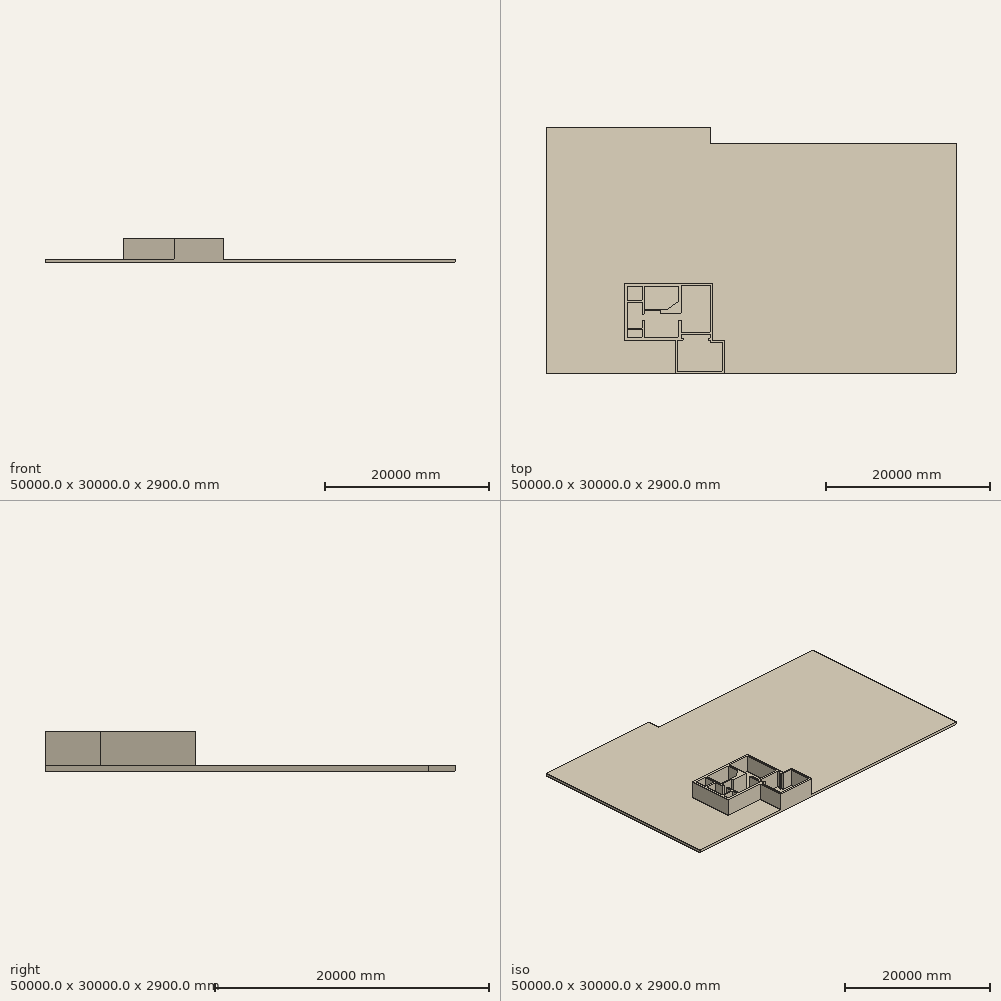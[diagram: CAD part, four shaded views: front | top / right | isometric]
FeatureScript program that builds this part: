
annotation { "Feature Type Name" : "Feature", "Feature Type Description" : "" }
export const myFeature = defineFeature(function(context is Context, id is Id, definition is map)
    precondition{}
    {
        {
            var Q0;
            Q0=qCreatedBy(makeId("Top.planeOp"),FACE);
            var sketch = newSketch(context, id + "F0", { "sketchPlane" : qUnion([Q0])});
            skLineSegment(sketch, "E0.bottom", {"start": v(-24996.8, 16240.64) * mm, "end": v(-4996.8, 16240.64) * mm});
            skLineSegment(sketch, "E0.top", {"start": v(-24996.8, -13759.36) * mm, "end": v(25003.2, -13759.36) * mm});
            skLineSegment(sketch, "E0.left", {"start": v(-24996.8, 16240.64) * mm, "end": v(-24996.8, -13759.36) * mm});
            skLineSegment(sketch, "E0.right", {"start": v(25003.2, 14240.64) * mm, "end": v(25003.2, -13759.36) * mm});
            skLineSegment(sketch, "E1", {"start": v(-4996.8, 16240.64) * mm, "end": v(-4996.8, 14240.64) * mm});
            skLineSegment(sketch, "E2", {"start": v(-4996.8, 14240.64) * mm, "end": v(25003.2, 14240.64) * mm});
            skSolve(sketch);
        }
        {
            var Q0;
            Q0 = qSketchRegion(id + "F0", true);
            extrude(context, id + "F1", {"entities" : qUnion([Q0]), "oppositeDirection" : true, "depth" : 400 * mm});
        }
        {
            var Q0;
            Q0=makeQuery(id+"F1.opExtrude","CAP_FACE",FACE,{"disambiguationData":[OSD([sQuery(id+"F0.wireOp",EDGE,"E0.bottom"),sQuery(id+"F0.wireOp",EDGE,"E0.top"),sQuery(id+"F0.wireOp",EDGE,"E0.left"),sQuery(id+"F0.wireOp",EDGE,"E0.right"),sQuery(id+"F0.wireOp",EDGE,"E1"),sQuery(id+"F0.wireOp",EDGE,"E2")])],"isStart":true});
            var sketch = newSketch(context, id + "F2", { "sketchPlane" : qUnion([Q0])});
            skLineSegment(sketch, "E3.bottom", {"start": v(-15496.8, -2759.36) * mm, "end": v(-8546.8, -2759.36) * mm});
            skLineSegment(sketch, "E3.top", {"start": v(-15496.8, -9759.36) * mm, "end": v(-8546.8, -9759.36) * mm});
            skLineSegment(sketch, "E3.left", {"start": v(-15496.8, -2759.36) * mm, "end": v(-15496.8, -9759.36) * mm});
            skLineSegment(sketch, "E3.right", {"start": v(-4796.8, -2759.36) * mm, "end": v(-4796.8, -9759.36) * mm});
            skLineSegment(sketch, "E4.bottom", {"start": v(-9246.8, -9759.36) * mm, "end": v(-8546.8, -9759.36) * mm});
            skLineSegment(sketch, "E4.top", {"start": v(-9246.8, -13759.36) * mm, "end": v(-3246.8, -13759.36) * mm});
            skLineSegment(sketch, "E4.left", {"start": v(-9246.8, -9759.36) * mm, "end": v(-9246.8, -13759.36) * mm});
            skLineSegment(sketch, "E4.right", {"start": v(-3246.8, -9759.36) * mm, "end": v(-3246.8, -13759.36) * mm});
            skLineSegment(sketch, "E5", {"start": v(-8546.8, -3009.36) * mm, "end": v(-8546.8, -6409.36) * mm});
            skLineSegment(sketch, "E6.trimOffspring", {"start": v(-4796.8, -9759.36) * mm, "end": v(-3246.8, -9759.36) * mm});
            skLineSegment(sketch, "E7.0", {"start": v(-15146.8, -3109.36) * mm, "end": v(-13346.8, -3109.36) * mm});
            skLineSegment(sketch, "E7.1", {"start": v(-15146.8, -3109.36) * mm, "end": v(-15146.8, -4909.36) * mm});
            skLineSegment(sketch, "E7.2", {"start": v(-15146.8, -9409.36) * mm, "end": v(-13346.8, -9409.36) * mm});
            skLineSegment(sketch, "E7.3", {"start": v(-8896.8, -3109.36) * mm, "end": v(-8896.8, -6409.36) * mm});
            skLineSegment(sketch, "E8", {"start": v(-8546.8, -2759.36) * mm, "end": v(-4796.8, -2759.36) * mm});
            skLineSegment(sketch, "E9.0", {"start": v(-5046.8, -3009.36) * mm, "end": v(-5046.8, -8759.36) * mm});
            skLineSegment(sketch, "E9.1", {"start": v(-5046.8, -3009.36) * mm, "end": v(-4570.48, -3009.36) * mm});
            skLineSegment(sketch, "E10.bottom", {"start": v(-8546.8, -9759.36) * mm, "end": v(-8346.8, -9759.36) * mm});
            skLineSegment(sketch, "E10.top", {"start": v(-8546.8, -9509.36) * mm, "end": v(-8346.8, -9509.36) * mm});
            skLineSegment(sketch, "E10.right", {"start": v(-8346.8, -9759.36) * mm, "end": v(-8346.8, -9509.36) * mm});
            skLineSegment(sketch, "E11.bottom", {"start": v(-5046.8, -9759.36) * mm, "end": v(-5246.8, -9759.36) * mm});
            skLineSegment(sketch, "E11.top", {"start": v(-5046.8, -9509.36) * mm, "end": v(-5246.8, -9509.36) * mm});
            skLineSegment(sketch, "E11.right", {"start": v(-5246.8, -9759.36) * mm, "end": v(-5246.8, -9509.36) * mm});
            skLineSegment(sketch, "E12", {"start": v(-5046.8, -8959.36) * mm, "end": v(-8546.8, -8959.36) * mm});
            skLineSegment(sketch, "E13", {"start": v(-8546.8, -8759.36) * mm, "end": v(-5046.8, -8759.36) * mm});
            skLineSegment(sketch, "E14.0", {"start": v(-5046.8, -10009.36) * mm, "end": v(-4796.8, -10009.36) * mm});
            skLineSegment(sketch, "E14.1", {"start": v(-8996.8, -9759.36) * mm, "end": v(-8996.8, -13509.36) * mm});
            skLineSegment(sketch, "E14.2", {"start": v(-8996.8, -13509.36) * mm, "end": v(-3496.8, -13509.36) * mm});
            skLineSegment(sketch, "E14.3", {"start": v(-3496.8, -10009.36) * mm, "end": v(-3496.8, -13509.36) * mm});
            skLineSegment(sketch, "E14.4", {"start": v(-4796.8, -10009.36) * mm, "end": v(-3496.8, -10009.36) * mm});
            skLineSegment(sketch, "E15", {"start": v(-5046.8, -10009.36) * mm, "end": v(-5046.8, -9759.36) * mm});
            skLineSegment(sketch, "E16", {"start": v(-5046.8, -3009.36) * mm, "end": v(-8546.8, -3009.36) * mm});
            skLineSegment(sketch, "E17", {"start": v(-8896.8, -6409.36) * mm, "end": v(-11146.8, -6409.36) * mm});
            skLineSegment(sketch, "E18", {"start": v(-11146.8, -6409.36) * mm, "end": v(-11146.8, -6049.36) * mm});
            skLineSegment(sketch, "E19", {"start": v(-11146.8, -6049.36) * mm, "end": v(-13096.8, -6049.36) * mm});
            skLineSegment(sketch, "E20", {"start": v(-13096.8, -6049.36) * mm, "end": v(-13096.8, -6521.46) * mm});
            skLineSegment(sketch, "E21", {"start": v(-13096.8, -8109.36) * mm, "end": v(-12196.8, -8109.36) * mm});
            skLineSegment(sketch, "E22", {"start": v(-12196.8, -8109.36) * mm, "end": v(-12196.8, -9409.36) * mm});
            skLineSegment(sketch, "E23", {"start": v(-8896.8, -6409.36) * mm, "end": v(-8546.8, -6409.36) * mm});
            skLineSegment(sketch, "E24", {"start": v(-8896.8, -7309.36) * mm, "end": v(-8546.8, -7309.36) * mm});
            skLineSegment(sketch, "E25.trimOffspring", {"start": v(-8546.8, -7309.36) * mm, "end": v(-8546.8, -8759.36) * mm});
            skLineSegment(sketch, "E26.trimOffspring", {"start": v(-8896.8, -7309.36) * mm, "end": v(-8896.8, -9409.36) * mm});
            skLineSegment(sketch, "E27", {"start": v(-13096.8, -3109.36) * mm, "end": v(-13096.8, -5899.36) * mm});
            skLineSegment(sketch, "E28", {"start": v(-13096.8, -5899.36) * mm, "end": v(-10154.4, -5899.36) * mm});
            skLineSegment(sketch, "E29", {"start": v(-10154.4, -5899.36) * mm, "end": v(-8896.8, -5005.93) * mm});
            skLineSegment(sketch, "E30", {"start": v(-15146.8, -4909.36) * mm, "end": v(-13346.8, -4909.36) * mm});
            skLineSegment(sketch, "E31", {"start": v(-13346.8, -3109.36) * mm, "end": v(-13346.8, -4909.36) * mm});
            skLineSegment(sketch, "E32", {"start": v(-13346.8, -6521.46) * mm, "end": v(-13096.8, -6521.46) * mm});
            skLineSegment(sketch, "E33", {"start": v(-13346.8, -7286.18) * mm, "end": v(-13096.8, -7286.18) * mm});
            skLineSegment(sketch, "E34.trimOffspring", {"start": v(-13346.8, -7286.18) * mm, "end": v(-13346.8, -8259.36) * mm});
            skLineSegment(sketch, "E35.trimOffspring", {"start": v(-13096.8, -7286.18) * mm, "end": v(-13096.8, -9409.36) * mm});
            skLineSegment(sketch, "E36", {"start": v(-15146.8, -5159.36) * mm, "end": v(-13346.8, -5159.36) * mm});
            skLineSegment(sketch, "E37", {"start": v(-13346.8, -8409.36) * mm, "end": v(-15146.8, -8409.36) * mm});
            skLineSegment(sketch, "E38", {"start": v(-15146.8, -8259.36) * mm, "end": v(-13346.8, -8259.36) * mm});
            skLineSegment(sketch, "E39.trimOffspring", {"start": v(-13346.8, -8409.36) * mm, "end": v(-13346.8, -9409.36) * mm});
            skLineSegment(sketch, "E40.trimOffspring", {"start": v(-15146.8, -8409.36) * mm, "end": v(-15146.8, -9409.36) * mm});
            skLineSegment(sketch, "E41.trimOffspring", {"start": v(-13096.8, -9409.36) * mm, "end": v(-8896.8, -9409.36) * mm});
            skLineSegment(sketch, "E42.trimOffspring", {"start": v(-13096.8, -3109.36) * mm, "end": v(-8896.8, -3109.36) * mm});
            skLineSegment(sketch, "E43.trimOffspring", {"start": v(-15146.8, -5159.36) * mm, "end": v(-15146.8, -8259.36) * mm});
            skLineSegment(sketch, "E44.trimOffspring", {"start": v(-13346.8, -5159.36) * mm, "end": v(-13346.8, -6521.46) * mm});
            skLineSegment(sketch, "E45.trimOffspring", {"start": v(-8546.8, -8959.36) * mm, "end": v(-8546.8, -9509.36) * mm});
            skLineSegment(sketch, "E46.trimOffspring", {"start": v(-5046.8, -8959.36) * mm, "end": v(-5046.8, -9509.36) * mm});
            skSolve(sketch);
        }
        {
            var Q0;
            {var subQ1=sQuery(id+"F2.wireOp",EDGE,"E3.bottom");Q0=makeQuery(id+"F2.imprint","IMPRINT",FACE,{"disambiguationData":[TD([[makeQuery(id+"F2.imprint","IMPRINT",EDGE,{"derivedFrom":subQ1}),-1.0]])]});}
            var Q1;
            Q1=makeQuery(id+"F2.imprint","IMPRINT",FACE,{"disambiguationData":[TD([[makeQuery(id+"F2.imprint","IMPRINT",EDGE,{"derivedFrom":sQuery(id+"F2.wireOp",EDGE,"E4.top")}),1.0]])]});
            var Q2;
            {var subQ6=sQuery(id+"F2.wireOp",EDGE,"6GIlhgQf-U01w-udwx-BTqk-wJ5JnaWOdKvH");Q2=makeQuery(id+"F2.imprint","IMPRINT",FACE,{"disambiguationData":[TD([[makeQuery(id+"F2.imprint","IMPRINT",EDGE,{"derivedFrom":subQ6}),1.0]])]});}
            var Q3;
            {var subQ0=sQuery(id+"F2.wireOp",EDGE,"E12");Q3=makeQuery(id+"F2.imprint","IMPRINT",FACE,{"disambiguationData":[TD([[makeQuery(id+"F2.imprint","IMPRINT",EDGE,{"derivedFrom":subQ0}),-1.0]])]});}
            var Q4;
            {var subQ0=sQuery(id+"F2.wireOp",EDGE,"E8");Q4=makeQuery(id+"F2.imprint","IMPRINT",FACE,{"disambiguationData":[TD([[makeQuery(id+"F2.imprint","IMPRINT",EDGE,{"derivedFrom":subQ0}),-1.0]])]});}
            extrude(context, id + "F3", {"entities" : qUnion([Q0, Q1, Q2, Q3, Q4]), "operationType" : NewBodyOperationType.ADD, "depth" : 2500 * mm});
        }
    });
